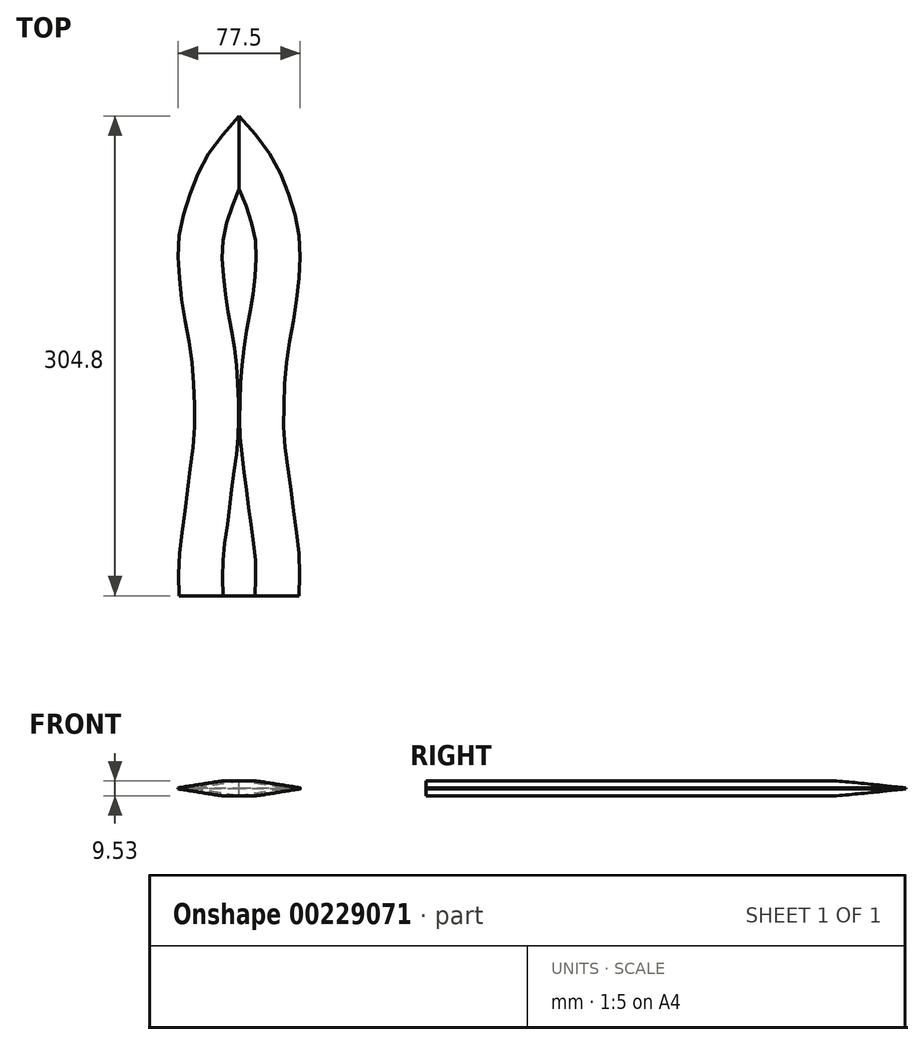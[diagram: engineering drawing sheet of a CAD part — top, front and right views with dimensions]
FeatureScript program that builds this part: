
annotation { "Feature Type Name" : "Feature", "Feature Type Description" : "" }
export const myFeature = defineFeature(function(context is Context, id is Id, definition is map)
    precondition{}
    {
        {
            var Q0;
            Q0=qCreatedBy(makeId("Top.planeOp"),FACE);
            var sketch = newSketch(context, id + "F0", { "sketchPlane" : qUnion([Q0])});
            skLineSegment(sketch, "E0", {"start": v(0, 254) * mm, "end": v(0, -254) * mm, "construction": true});
            skPoint(sketch, "E1", {"position": v(0, 0) * mm});
            skLineSegment(sketch, "E2", {"start": v(-38.1, 254) * mm, "end": v(38.1, 254) * mm, "construction": true});
            skLineSegment(sketch, "E3", {"start": v(-38.1, -50.8) * mm, "end": v(38.1, -50.8) * mm, "construction": true});
            skPoint(sketch, "E4", {"position": v(0, 254) * mm});
            skPoint(sketch, "E5", {"position": v(0, -50.8) * mm});
            skSolve(sketch);
        }
        {
            var Q0;
            Q0=qCreatedBy(makeId("Top.planeOp"),FACE);
            var sketch = newSketch(context, id + "F1", { "sketchPlane" : qUnion([Q0])});
            skLineSegment(sketch, "E6", {"start": v(-20.32, 228.6) * mm, "end": v(20.32, 228.6) * mm, "construction": true});
            skLineSegment(sketch, "E7", {"start": v(31.75, 203.2) * mm, "end": v(-31.75, 203.2) * mm, "construction": true});
            skLineSegment(sketch, "E8", {"start": v(-38.1, 177.8) * mm, "end": v(38.1, 177.8) * mm, "construction": true});
            skLineSegment(sketch, "E9", {"start": v(38.1, 152.4) * mm, "end": v(-38.1, 152.4) * mm, "construction": true});
            skLineSegment(sketch, "E10", {"start": v(-34.93, 127) * mm, "end": v(34.93, 127) * mm, "construction": true});
            skLineSegment(sketch, "E11", {"start": v(30.48, 101.6) * mm, "end": v(-30.48, 101.6) * mm, "construction": true});
            skLineSegment(sketch, "E12", {"start": v(-28.58, 76.2) * mm, "end": v(28.58, 76.2) * mm, "construction": true});
            skPoint(sketch, "E13", {"position": v(0, 228.6) * mm});
            skPoint(sketch, "E14", {"position": v(0, 203.2) * mm});
            skPoint(sketch, "E15", {"position": v(0, 177.8) * mm});
            skPoint(sketch, "E16", {"position": v(0, 152.4) * mm});
            skPoint(sketch, "E17", {"position": v(0, 127) * mm});
            skPoint(sketch, "E18", {"position": v(0, 101.6) * mm});
            skPoint(sketch, "E19", {"position": v(0, 76.2) * mm});
            skLineSegment(sketch, "E20", {"start": v(-21.26, 254) * mm, "end": v(21.26, 254) * mm, "construction": true});
            skPoint(sketch, "E21", {"position": v(0, 254) * mm});
            skLineSegment(sketch, "E22", {"start": v(-28.58, 50.8) * mm, "end": v(28.58, 50.8) * mm, "construction": true});
            skLineSegment(sketch, "E23", {"start": v(-31.75, 25.4) * mm, "end": v(31.75, 25.4) * mm, "construction": true});
            skLineSegment(sketch, "E24", {"start": v(-34.93, 0) * mm, "end": v(34.93, 0) * mm, "construction": true});
            skLineSegment(sketch, "E25", {"start": v(-38.1, -25.4) * mm, "end": v(38.1, -25.4) * mm, "construction": true});
            skLineSegment(sketch, "E26", {"start": v(-38.1, -50.8) * mm, "end": v(38.1, -50.8) * mm});
            skPoint(sketch, "E27", {"position": v(0, 50.8) * mm});
            skPoint(sketch, "E28", {"position": v(0, 25.4) * mm});
            skPoint(sketch, "E29", {"position": v(0, 0) * mm});
            skPoint(sketch, "E30", {"position": v(0, -25.4) * mm});
            skPoint(sketch, "E31", {"position": v(0, -50.8) * mm});
            skFitSpline(sketch, "E32", {"points": [v(0, 254) * mm, v(20.32, 228.6) * mm, v(31.75, 203.2) * mm, v(38.1, 177.8) * mm, v(38.1, 152.4) * mm, v(34.92, 127) * mm, v(30.48, 101.6) * mm, v(28.58, 76.2) * mm, v(28.57, 50.8) * mm, v(31.75, 25.4) * mm, v(34.93, 0) * mm, v(38.1, -25.4) * mm, v(38.1, -50.8) * mm], "startDerivative": vector(240.53, -268.87) * mm, "endDerivative": vector(-6.15, -310.53) * mm});
            skFitSpline(sketch, "E33.MirrorCS", {"points": [v(0, 254) * mm, v(-20.32, 228.6) * mm, v(-31.75, 203.2) * mm, v(-38.1, 177.8) * mm, v(-38.1, 152.4) * mm, v(-34.92, 127) * mm, v(-30.48, 101.6) * mm, v(-28.58, 76.2) * mm, v(-28.57, 50.8) * mm, v(-31.75, 25.4) * mm, v(-34.93, 0) * mm, v(-38.1, -25.4) * mm, v(-38.1, -50.8) * mm], "startDerivative": vector(-240.53, -268.87) * mm, "endDerivative": vector(6.15, -310.53) * mm});
            skSolve(sketch);
        }
        {
            var Q0;
            Q0 = qSketchRegion(id + "F1", true);
            extrude(context, id + "F2", {"entities" : qUnion([Q0]), "depth" : 9.52 * mm});
        }
        {
            var Q0;
            Q0=makeQuery(id+"F2.opExtrude","CAP_EDGE",EDGE,{"disambiguationData":[OSD([sQuery(id+"F1.wireOp",EDGE,"E32")])],"isStart":false});
            var Q1;
            Q1=makeQuery(id+"F2.opExtrude","CAP_EDGE",EDGE,{"disambiguationData":[OSD([sQuery(id+"F1.wireOp",EDGE,"E32")])],"isStart":true});
            var Q2;
            Q2=makeQuery(id+"F2.opExtrude","CAP_EDGE",EDGE,{"disambiguationData":[OSD([sQuery(id+"F1.wireOp",EDGE,"E33.MirrorCS")])],"isStart":false});
            var Q3;
            Q3=makeQuery(id+"F2.opExtrude","CAP_EDGE",EDGE,{"disambiguationData":[OSD([sQuery(id+"F1.wireOp",EDGE,"E33.MirrorCS")])],"isStart":true});
            chamfer(context, id + "F3", {"entities" : qUnion([Q0, Q1, Q2, Q3]), "chamferType" : ChamferType.OFFSET_ANGLE, "width" : 27.94 * mm, "oppositeDirection" : true, "angle" : 9 * degree, "tangentPropagation" : true});
        }
        {
            var Q0;
            Q0=qCreatedBy(makeId("Top.planeOp"),FACE);
            cPlane(context, id + "F4", {"entities" : qUnion([Q0]), "cplaneType" : CPlaneType.OFFSET, "offset" : 12.7 * mm, "width" : 152.4 * mm, "height" : 152.4 * mm});
        }
    });
